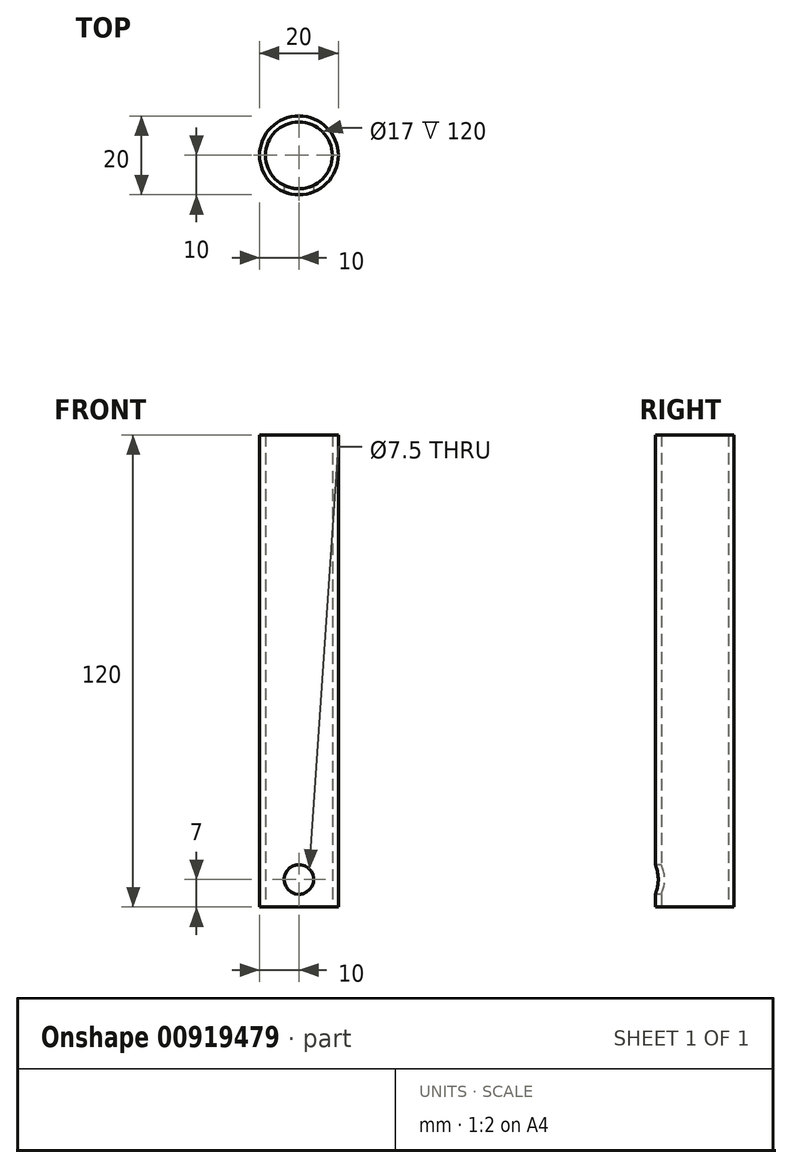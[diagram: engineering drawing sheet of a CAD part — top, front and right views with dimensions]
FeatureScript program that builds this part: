
annotation { "Feature Type Name" : "Feature", "Feature Type Description" : "" }
export const myFeature = defineFeature(function(context is Context, id is Id, definition is map)
    precondition{}
    {
        {
            var Q0;
            Q0=qCreatedBy(makeId("Top.planeOp"),FACE);
            var sketch = newSketch(context, id + "F0", { "sketchPlane" : qUnion([Q0])});
            skCircle(sketch, "E0", {"center": v(0, 0) * mm, "radius": 10 * mm});
            skCircle(sketch, "E1", {"center": v(0, 0) * mm, "radius": 8.5 * mm});
            skSolve(sketch);
        }
        {
            var Q0;
            Q0=qSketchRegion(id+"F0",true);
            extrude(context, id + "F1", {"entities" : qUnion([Q0]), "depth" : 120 * mm, "offsetDistance" : 25 * mm});
        }
        {
            var Q0;
            Q0=qCreatedBy(makeId("Front.planeOp"),FACE);
            cPlane(context, id + "F2", {"entities" : qUnion([Q0]), "cplaneType" : CPlaneType.OFFSET, "offset" : 10 * mm, "width" : 150 * mm, "height" : 150 * mm});
        }
        {
            var Q0;
            Q0=qCreatedBy(id+"F2.planeOp",FACE);
            var sketch = newSketch(context, id + "F3", { "sketchPlane" : qUnion([Q0])});
            skCircle(sketch, "E2", {"center": v(0, 7) * mm, "radius": 3.75 * mm});
            skSolve(sketch);
        }
        {
            var Q0;
            Q0 = qSketchRegion(id + "F3", true);
            var Q1;
            Q1=makeQuery(id+"F1.opExtrude","SWEPT_FACE",FACE,{"disambiguationData":[OSD([sQuery(id+"F0.wireOp",EDGE,"E1")])]});
            extrude(context, id + "F4", {"entities" : qUnion([Q0]), "operationType" : NewBodyOperationType.REMOVE, "endBound" : BoundingType.UP_TO_SURFACE, "oppositeDirection" : true, "depth" : 25 * mm, "endBoundEntityFace" : qUnion([Q1]), "offsetDistance" : 25 * mm});
        }
    });
